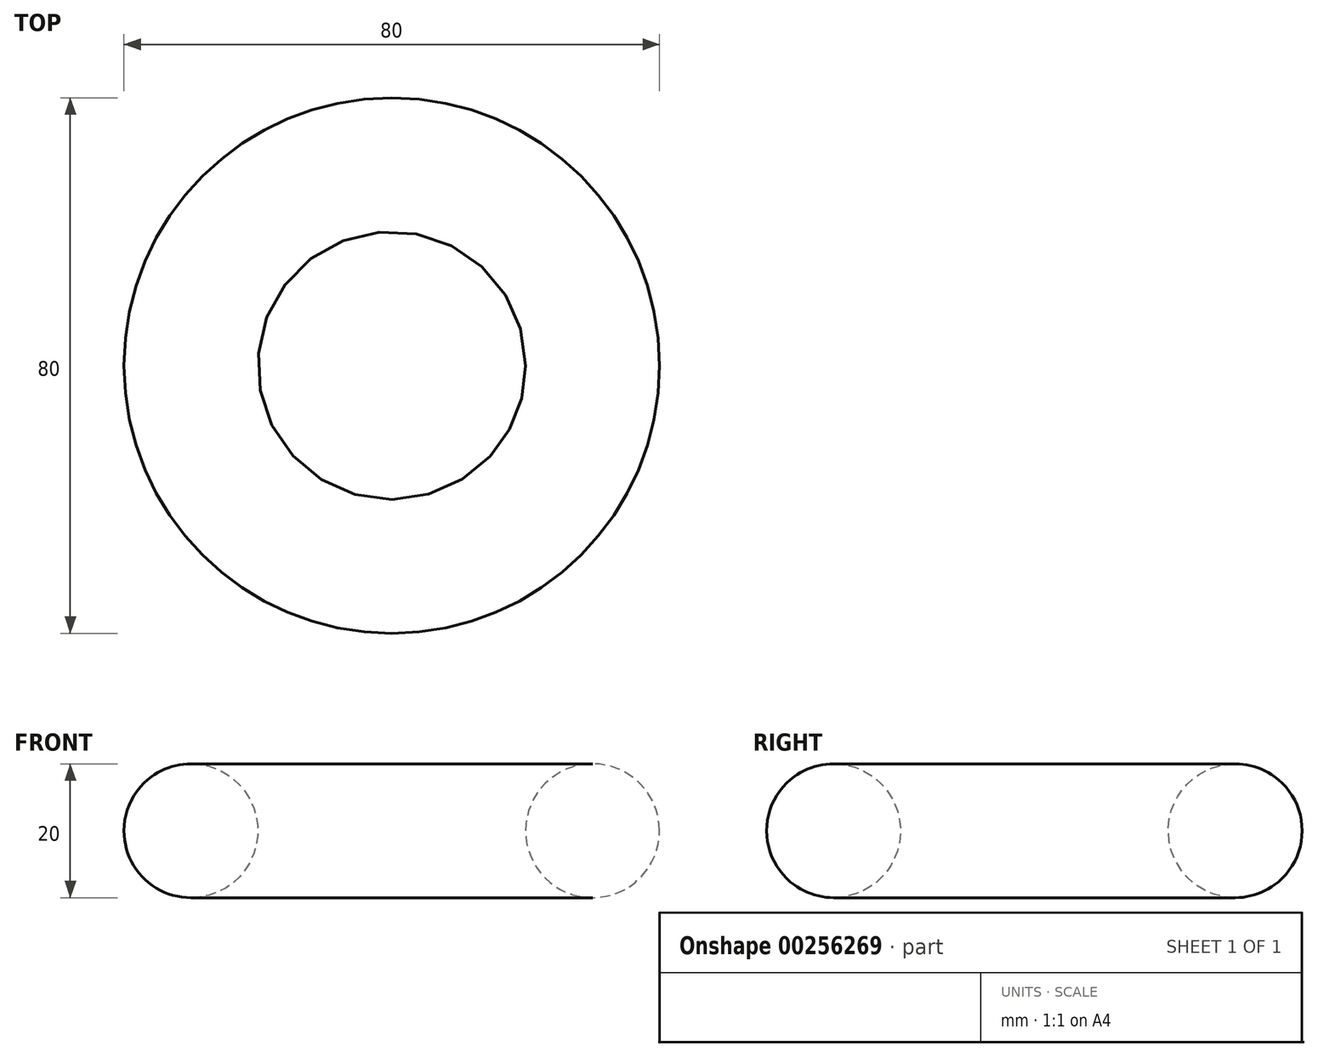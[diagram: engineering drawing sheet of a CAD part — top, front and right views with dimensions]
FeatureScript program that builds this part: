
annotation { "Feature Type Name" : "Feature", "Feature Type Description" : "" }
export const myFeature = defineFeature(function(context is Context, id is Id, definition is map)
    precondition{}
    {
        {
            var Q0;
            Q0=qCreatedBy(makeId("Front.planeOp"),FACE);
            var sketch = newSketch(context, id + "F0", { "sketchPlane" : qUnion([Q0])});
            skCircle(sketch, "E0", {"center": v(28553.52, 0) * mm, "radius": 10000 * mm});
            skCircle(sketch, "E1", {"center": v(30, 0) * mm, "radius": 10 * mm});
            skLineSegment(sketch, "E2", {"start": v(0, 25.1) * mm, "end": v(0, -40.6) * mm, "construction": true});
            skSolve(sketch);
        }
        {
            var Q0;
            Q0=makeQuery(id+"F0.imprint","IMPRINT",FACE,{"disambiguationData":[TD([[makeQuery(id+"F0.imprint","IMPRINT",EDGE,{"derivedFrom":sQuery(id+"F0.wireOp",EDGE,"E1")}),1.0]])]});
            var Q1;
            Q1=sQuery(id+"F0.wireOp",EDGE,"E2");
            revolve(context, id + "F1", {"entities" : qUnion([Q0]), "axis" : qUnion([Q1]), "revolveType" : RevolveType.FULL});
        }
    });
